# Revit family: QF_Turbo Air_TGF-5SD
name_source: partatom
category: Specialty Equipment
revit_build: Autodesk Revit MEP 2012 (Build: 20110916_2132(x64)
units: mm (PartAtom-declared; Revit-internal decimal feet)

## types (3) — shared parameters
Apparent Power = 633 VA
Assembly Code = E1090320
CSI MasterFormat = 11 41 13
Conn Plug = NEMA 5-15P
Cycle = 60 Hz
Depth = 1' - 10 13/16"
Description = Freezer Merchandiser
Elec Conn Connection Height = 0' - 2 11/16"
FL Amps = 6 A
Foodservice Equipment Identifier = Yes
HP = 1/3
Height = 2' - 8 3/4"
Manufacturer = Turbo Air
Phase = 1
URL = www.turboairinc.com
Volts = 115 V
Weight in Pounds = 195
Width = 2' - 1"

## per-type parameters (varying)
| type | Body Material | Door Material | Model |
| Black | QF_Finishes_Black | QF_Finishes_Black | TGF-5SDB |
| White | QF_Finishes_White | QF_Finishes_White | TGF-5SDW |
| White - Wine | QF_Finishes_White | QF_Finishes_Anodized - Red | TGF-5SDV |

## geometry (parser evidence)
native form markers: Blend x26, Sweep x5
no freeform markers — native parametric forms only
